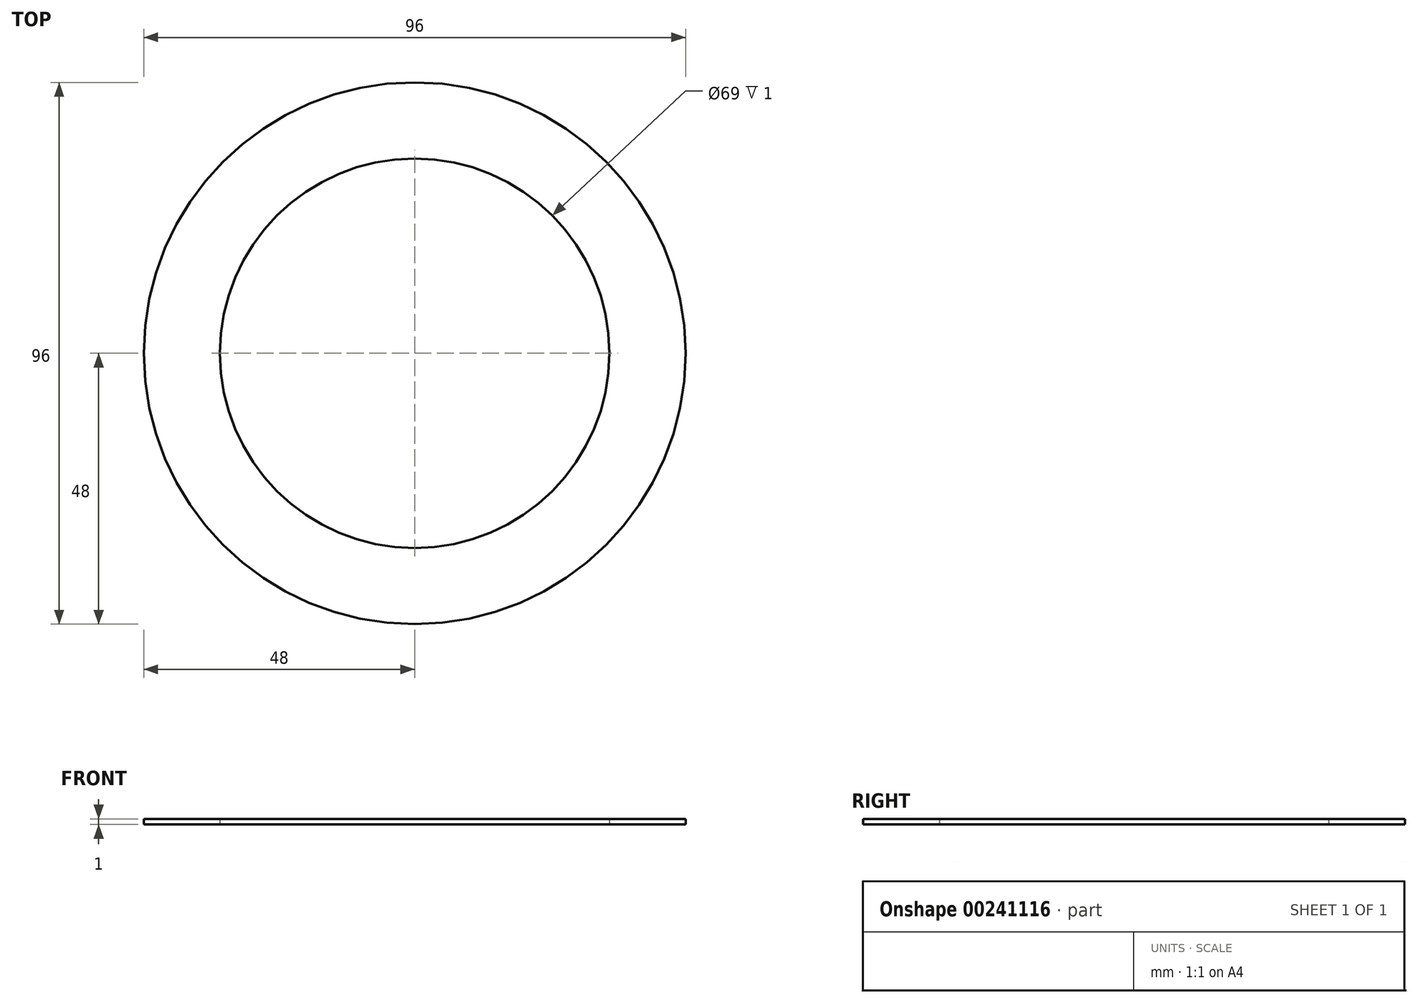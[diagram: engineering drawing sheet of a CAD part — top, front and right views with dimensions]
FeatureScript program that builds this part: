
annotation { "Feature Type Name" : "Feature", "Feature Type Description" : "" }
export const myFeature = defineFeature(function(context is Context, id is Id, definition is map)
    precondition{}
    {
        {
            var Q0;
            Q0=qCreatedBy(makeId("Top.planeOp"),FACE);
            var sketch = newSketch(context, id + "F0", { "sketchPlane" : qUnion([Q0])});
            skCircle(sketch, "E0", {"center": v(0, 0) * mm, "radius": 48 * mm});
            skCircle(sketch, "E1", {"center": v(0, 0) * mm, "radius": 34.5 * mm});
            skSolve(sketch);
        }
        {
            var Q0;
            Q0 = qSketchRegion(id + "F0", true);
            extrude(context, id + "F1", {"entities" : qUnion([Q0]), "depth" : 1 * mm});
        }
    });
